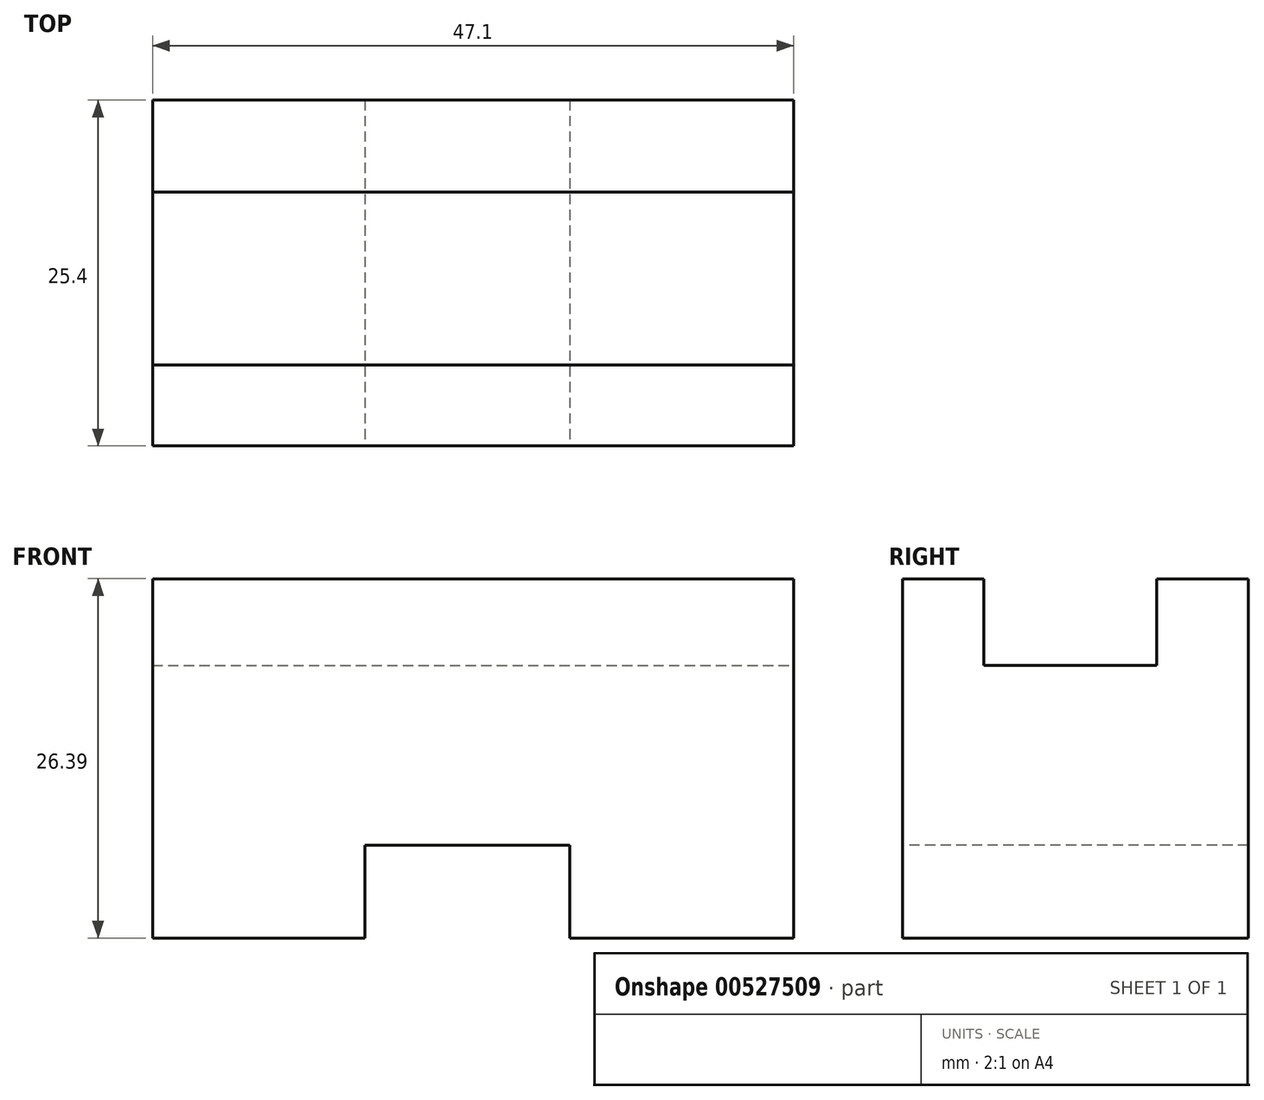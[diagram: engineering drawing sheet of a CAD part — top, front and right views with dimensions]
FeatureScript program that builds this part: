
annotation { "Feature Type Name" : "Feature", "Feature Type Description" : "" }
export const myFeature = defineFeature(function(context is Context, id is Id, definition is map)
    precondition{}
    {
        {
            var Q0;
            Q0=qCreatedBy(makeId("Front.planeOp"),FACE);
            var sketch = newSketch(context, id + "F0", { "sketchPlane" : qUnion([Q0])});
            skLineSegment(sketch, "E0", {"start": v(0, 0) * mm, "end": v(15.6, 0) * mm});
            skLineSegment(sketch, "E1", {"start": v(15.6, 0) * mm, "end": v(15.6, 6.8) * mm});
            skLineSegment(sketch, "E2", {"start": v(15.6, 6.8) * mm, "end": v(30.64, 6.8) * mm});
            skLineSegment(sketch, "E3", {"start": v(30.64, 6.8) * mm, "end": v(30.64, 0) * mm});
            skLineSegment(sketch, "E4", {"start": v(30.64, 0) * mm, "end": v(47.1, 0) * mm});
            skLineSegment(sketch, "E5", {"start": v(47.1, 26.39) * mm, "end": v(47.1, 0) * mm});
            skLineSegment(sketch, "E6", {"start": v(47.1, 26.39) * mm, "end": v(0, 26.39) * mm});
            skLineSegment(sketch, "E7", {"start": v(0, 26.39) * mm, "end": v(0, 0) * mm});
            skSolve(sketch);
        }
        {
            var Q0;
            Q0=makeQuery(id+"F0.imprint","IMPRINT",FACE,{"disambiguationData":[TD([[makeQuery(id+"F0.imprint","IMPRINT",EDGE,{"derivedFrom":sQuery(id+"F0.wireOp",EDGE,"E0")}),1.0]])]});
            extrude(context, id + "F1", {"entities" : qUnion([Q0]), "oppositeDirection" : true, "depth" : 25.4 * mm, "offsetDistance" : 25.4 * mm});
        }
        {
            var Q0;
            Q0=makeQuery(id+"F1.opExtrude","SWEPT_FACE",FACE,{"disambiguationData":[OSD([sQuery(id+"F0.wireOp",EDGE,"E6")])]});
            var sketch = newSketch(context, id + "F2", { "sketchPlane" : qUnion([Q0])});
            skLineSegment(sketch, "E8", {"start": v(0, 18.66) * mm, "end": v(47.1, 18.66) * mm});
            skLineSegment(sketch, "E9", {"start": v(47.1, 18.66) * mm, "end": v(47.1, 5.96) * mm});
            skLineSegment(sketch, "E10", {"start": v(47.1, 5.96) * mm, "end": v(0, 5.96) * mm});
            skLineSegment(sketch, "E11", {"start": v(0, 5.96) * mm, "end": v(0, 18.66) * mm});
            skSolve(sketch);
        }
        {
            var Q0;
            Q0=makeQuery(id+"F2.imprint","IMPRINT",FACE,{"disambiguationData":[TD([[makeQuery(id+"F2.imprint","IMPRINT",EDGE,{"derivedFrom":sQuery(id+"F2.wireOp",EDGE,"E8")}),-1.0]])]});
            extrude(context, id + "F3", {"entities" : qUnion([Q0]), "operationType" : NewBodyOperationType.REMOVE, "oppositeDirection" : true, "depth" : 6.35 * mm, "offsetDistance" : 25.4 * mm});
        }
    });
